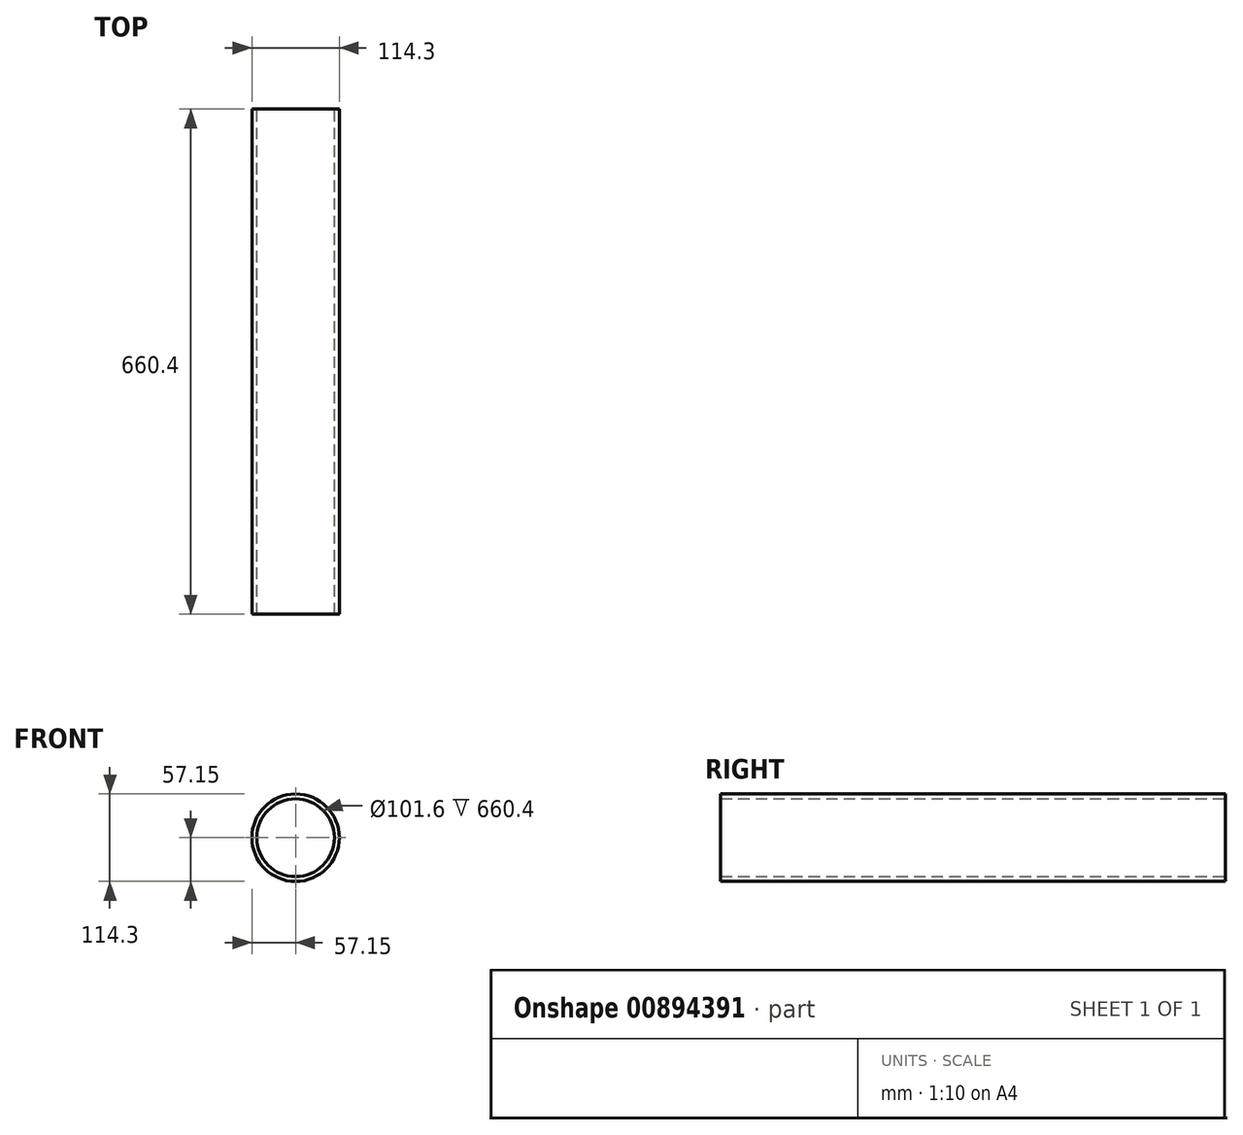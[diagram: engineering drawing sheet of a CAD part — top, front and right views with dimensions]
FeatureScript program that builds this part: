
annotation { "Feature Type Name" : "Feature", "Feature Type Description" : "" }
export const myFeature = defineFeature(function(context is Context, id is Id, definition is map)
    precondition{}
    {
        {
            var Q0;
            Q0=qCreatedBy(makeId("Front.planeOp"), FACE);
            var sketch = newSketch(context, id + "F0", { "sketchPlane" : qUnion([Q0])});
            skCircle(sketch, "E0", {"center": v(0, 0) * mm, "radius": 57.15 * mm});
            skCircle(sketch, "E1", {"center": v(0, 0) * mm, "radius": 50.8 * mm});
            skSolve(sketch);
        }
        {
            var Q0;
            Q0 = qSketchRegion(id + "F0", true);
            extrude(context, id + "F1", {"entities" : qUnion([Q0]), "depth" : 660.4 * mm, "offsetDistance" : 25.4 * mm});
        }
    });
